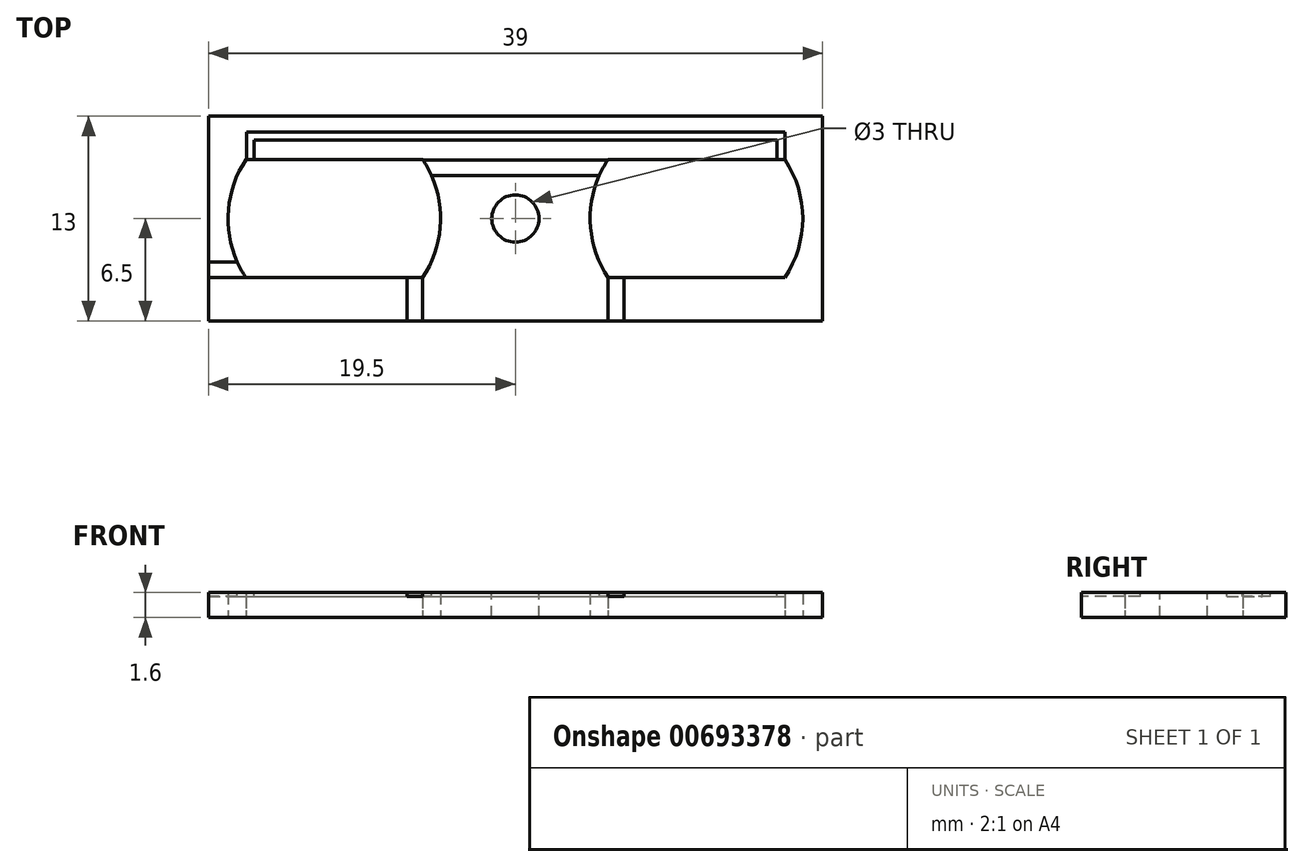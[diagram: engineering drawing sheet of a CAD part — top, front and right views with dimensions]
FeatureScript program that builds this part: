
annotation { "Feature Type Name" : "Feature", "Feature Type Description" : "" }
export const myFeature = defineFeature(function(context is Context, id is Id, definition is map)
    precondition{}
    {
        {
            var Q0;
            Q0=qCreatedBy(makeId("Top.planeOp"),FACE);
            var sketch = newSketch(context, id + "F0", { "sketchPlane" : qUnion([Q0])});
            skLineSegment(sketch, "E0.bottom", {"start": v(-19.5, 6.5) * mm, "end": v(19.5, 6.5) * mm});
            skLineSegment(sketch, "E0.top", {"start": v(-19.5, -6.5) * mm, "end": v(19.5, -6.5) * mm});
            skLineSegment(sketch, "E0.left", {"start": v(-19.5, 6.5) * mm, "end": v(-19.5, -6.5) * mm});
            skLineSegment(sketch, "E0.right", {"start": v(19.5, 6.5) * mm, "end": v(19.5, -6.5) * mm});
            skLineSegment(sketch, "E1.left", {"start": v(0, 0) * mm, "end": v(0, 0) * mm});
            skArc(sketch, "E2", {"start": v(-5.89, -3.75) * mm, "mid": v(-4.75, 0) * mm, "end": v(-5.89, 3.75) * mm});
            skArc(sketch, "E3", {"start": v(5.89, 3.75) * mm, "mid": v(4.75, 0) * mm, "end": v(5.89, -3.75) * mm});
            skLineSegment(sketch, "E4", {"start": v(-17.11, 3.75) * mm, "end": v(-5.89, 3.75) * mm});
            skLineSegment(sketch, "E5", {"start": v(-17.11, -3.75) * mm, "end": v(-5.89, -3.75) * mm});
            skLineSegment(sketch, "E6.trimOffspring", {"start": v(5.89, 3.75) * mm, "end": v(17.11, 3.75) * mm});
            skLineSegment(sketch, "E7.trimOffspring", {"start": v(5.89, -3.75) * mm, "end": v(17.11, -3.75) * mm});
            skArc(sketch, "E8.trimOffspring", {"start": v(-17.11, 3.75) * mm, "mid": v(-18.25, 0) * mm, "end": v(-17.11, -3.75) * mm});
            skArc(sketch, "E9.trimOffspring", {"start": v(17.11, -3.75) * mm, "mid": v(18.25, 0) * mm, "end": v(17.11, 3.75) * mm});
            skSolve(sketch);
        }
        {
            var Q0;
            Q0=makeQuery(id+"F0.imprint","IMPRINT",FACE,{"disambiguationData":[TD([[makeQuery(id+"F0.imprint","IMPRINT",EDGE,{"derivedFrom":sQuery(id+"F0.wireOp",EDGE,"E0.bottom")}),-1.0]])]});
            extrude(context, id + "F1", {"entities" : qUnion([Q0]), "depth" : 1.6 * mm, "offsetDistance" : 25 * mm});
        }
        {
            var Q0;
            Q0=makeQuery(id+"F1.opExtrude","CAP_FACE",FACE,{"disambiguationData":[OSD([sQuery(id+"F0.wireOp",EDGE,"E0.bottom"),sQuery(id+"F0.wireOp",EDGE,"E0.top"),sQuery(id+"F0.wireOp",EDGE,"E0.left"),sQuery(id+"F0.wireOp",EDGE,"E0.right"),sQuery(id+"F0.wireOp",EDGE,"E2"),sQuery(id+"F0.wireOp",EDGE,"E3"),sQuery(id+"F0.wireOp",EDGE,"E4"),sQuery(id+"F0.wireOp",EDGE,"E5"),sQuery(id+"F0.wireOp",EDGE,"E6.trimOffspring"),sQuery(id+"F0.wireOp",EDGE,"E7.trimOffspring"),sQuery(id+"F0.wireOp",EDGE,"E8.trimOffspring"),sQuery(id+"F0.wireOp",EDGE,"E9.trimOffspring")])],"isStart":false});
            var sketch = newSketch(context, id + "F2", { "sketchPlane" : qUnion([Q0])});
            skLineSegment(sketch, "E10", {"start": v(-19.5, -3.75) * mm, "end": v(-17.11, -3.75) * mm});
            skLineSegment(sketch, "E11", {"start": v(-17.66, -2.75) * mm, "end": v(-19.5, -2.75) * mm});
            skLineSegment(sketch, "E12.bottom", {"start": v(-6.89, -3.75) * mm, "end": v(-5.89, -3.75) * mm});
            skLineSegment(sketch, "E12.top", {"start": v(-6.89, -6.5) * mm, "end": v(-5.89, -6.5) * mm});
            skLineSegment(sketch, "E12.left", {"start": v(-6.89, -3.75) * mm, "end": v(-6.89, -6.5) * mm});
            skLineSegment(sketch, "E12.right", {"start": v(-5.89, -3.75) * mm, "end": v(-5.89, -6.5) * mm});
            skLineSegment(sketch, "E13.bottom", {"start": v(-5.88, 3.73) * mm, "end": v(5.88, 3.73) * mm});
            skLineSegment(sketch, "E13.top", {"start": v(-16.58, 5) * mm, "end": v(16.61, 5) * mm});
            skLineSegment(sketch, "E13.left", {"start": v(-16.58, 3.75) * mm, "end": v(-16.58, 5) * mm});
            skLineSegment(sketch, "E13.right", {"start": v(16.61, 3.75) * mm, "end": v(16.61, 5) * mm});
            skLineSegment(sketch, "E14", {"start": v(-5.33, 2.73) * mm, "end": v(5.33, 2.73) * mm});
            skLineSegment(sketch, "E15", {"start": v(-17.08, 3.75) * mm, "end": v(-17.08, 5.5) * mm});
            skLineSegment(sketch, "E16", {"start": v(-17.08, 5.5) * mm, "end": v(17.11, 5.5) * mm});
            skLineSegment(sketch, "E17", {"start": v(17.11, 5.5) * mm, "end": v(17.11, 3.75) * mm});
            skLineSegment(sketch, "E18.bottom", {"start": v(5.89, -3.75) * mm, "end": v(6.89, -3.75) * mm});
            skLineSegment(sketch, "E18.top", {"start": v(5.89, -6.5) * mm, "end": v(6.89, -6.5) * mm});
            skLineSegment(sketch, "E18.left", {"start": v(5.89, -3.75) * mm, "end": v(5.89, -6.5) * mm});
            skLineSegment(sketch, "E18.right", {"start": v(6.89, -3.75) * mm, "end": v(6.89, -6.5) * mm});
            skSolve(sketch);
        }
        {
            var Q0;
            Q0=makeQuery(id+"F2.imprint","IMPRINT",FACE,{"disambiguationData":[TD([[makeQuery(id+"F2.imprint","IMPRINT",EDGE,{"derivedFrom":sQuery(id+"F2.wireOp",EDGE,"E13.top")}),1.0]])]});
            var Q1;
            {var subQ0=sQuery(id+"F2.wireOp",EDGE,"E13.bottom");Q1=makeQuery(id+"F2.imprint","IMPRINT",FACE,{"disambiguationData":[TD([[makeQuery(id+"F2.imprint","IMPRINT",EDGE,{"derivedFrom":subQ0}),-1.0]])]});}
            var Q2;
            Q2=makeQuery(id+"F2.imprint","IMPRINT",FACE,{"disambiguationData":[TD([[makeQuery(id+"F2.imprint","IMPRINT",EDGE,{"derivedFrom":sQuery(id+"F2.wireOp",EDGE,"E12.bottom")}),-1.0]])]});
            var Q3;
            {var subQ0=sQuery(id+"F2.wireOp",EDGE,"E10");Q3=makeQuery(id+"F2.imprint","IMPRINT",FACE,{"disambiguationData":[TD([[makeQuery(id+"F2.imprint","IMPRINT",EDGE,{"derivedFrom":subQ0}),1.0]])]});}
            var Q4;
            Q4=makeQuery(id+"F2.imprint","IMPRINT",FACE,{"disambiguationData":[TD([[makeQuery(id+"F2.imprint","IMPRINT",EDGE,{"derivedFrom":sQuery(id+"F2.wireOp",EDGE,"E18.bottom")}),-1.0]])]});
            extrude(context, id + "F3", {"entities" : qUnion([Q0, Q1, Q2, Q3, Q4]), "operationType" : NewBodyOperationType.REMOVE, "oppositeDirection" : true, "depth" : .25 * mm, "offsetDistance" : 25 * mm});
        }
        {
            var Q0;
            {var subQ0=sQuery(id+"F0.wireOp",EDGE,"E3");var subQ1=sQuery(id+"F0.wireOp",EDGE,"E2");var subQ2=sQuery(id+"F0.wireOp",EDGE,"E0.top");Q0=makeQuery(id+"F3.boolean.opBoolean","SPLIT",FACE,{"disambiguationData":[TD([makeQuery(id+"F3.opExtrude","SWEPT_FACE",FACE,{"disambiguationData":[OSD([sQuery(id+"F2.wireOp",EDGE,"E12.right")])]})])],"derivedFrom":makeQuery(id+"F1.opExtrude","CAP_FACE",FACE,{"disambiguationData":[OSD([sQuery(id+"F0.wireOp",EDGE,"E0.bottom"),subQ2,sQuery(id+"F0.wireOp",EDGE,"E0.left"),sQuery(id+"F0.wireOp",EDGE,"E0.right"),subQ1,subQ0,sQuery(id+"F0.wireOp",EDGE,"E4"),sQuery(id+"F0.wireOp",EDGE,"E5"),sQuery(id+"F0.wireOp",EDGE,"E6.trimOffspring"),sQuery(id+"F0.wireOp",EDGE,"E7.trimOffspring"),sQuery(id+"F0.wireOp",EDGE,"E8.trimOffspring"),sQuery(id+"F0.wireOp",EDGE,"E9.trimOffspring")])],"isStart":false})});}
            var sketch = newSketch(context, id + "F4", { "sketchPlane" : qUnion([Q0])});
            skCircle(sketch, "E19", {"center": v(0, 0) * mm, "radius": 1.5 * mm});
            skSolve(sketch);
        }
        {
            var Q0;
            Q0=makeQuery(id+"F4.imprint","IMPRINT",FACE,{"disambiguationData":[TD([[makeQuery(id+"F4.imprint","IMPRINT",EDGE,{"derivedFrom":sQuery(id+"F4.wireOp",EDGE,"E19")}),1.0]])]});
            extrude(context, id + "F5", {"entities" : qUnion([Q0]), "operationType" : NewBodyOperationType.REMOVE, "endBound" : BoundingType.THROUGH_ALL, "oppositeDirection" : true, "depth" : 25 * mm, "offsetDistance" : 25 * mm});
        }
    });
